# Revit family: Bolt-Assembly-Steel & Tube-ISO Metric
name_source: partatom
category: Structural Connections
revit_build: Autodesk Revit 2017 (Build: 20171027_0315(x64)
units: mm (PartAtom-declared; Revit-internal decimal feet)

## family parameters
Cut with Voids When Loaded = No
Enable cutting in views = Yes
Host = Face
Material for Model Behavior = Steel
OmniClass Number = 23.20.40.11.14.27
Shared = Yes

## types (1)
- M16
    Arc Height = 2.202 mm
    Bolt Diameter = 16 mm  [stored 0.0524934 ft]
    Bolt Head = 10.18 mm  [stored 0.0333989 ft]
    CBICode = 3411
    CBIDescription = Structural steelwork
    Centreline Size = 48 mm
    Cove = 24 mm  [stored 0.0787402 ft]
    Default Elevation = 0 mm  [stored 0 ft]
    Description = ISO Metric Precision Hexagon Bolt in accordance with BS 3692:2001
    Height_ANZRS = 27.713 mm
    Manufacturer = Steel & Tube
    ManufacturerName = Steel & Tube
    ManufacturerURL = http://www.steelandtube.co.nz
    Material_ANZRS = Metal-Steel-450MPa
    Model = M16
    ModifiedIssue_ANZRS = 20160526 $
    Nut = 13 mm  [stored 0.0426509 ft]
    Nut Cross Section = 27.713 mm
    Nut Size = 24 mm  [stored 0.0787402 ft]
    SpecificationDescription = Steel & Tube Purlins & Girts
    SpecificationReference = 3411ST
    Type Comments = Bolt Assembly
    URL = http://www.steelandtube.co.nz
    Uniclass2015Code = Pr_20_76_51_21
    Uniclass2015Title = Cold-formed galvanized steel sections
    Uniclass2015Version = 2015
    Washer Diameter = 30 mm  [stored 0.0984252 ft]
    Width_ANZRS = 27.713 mm

note: [stored X ft] marks values corroborated as IEEE doubles in the binary element streams (Revit-internal decimal feet)

## geometry (parser evidence)
native form markers: Sweep x2
no freeform markers — native parametric forms only
